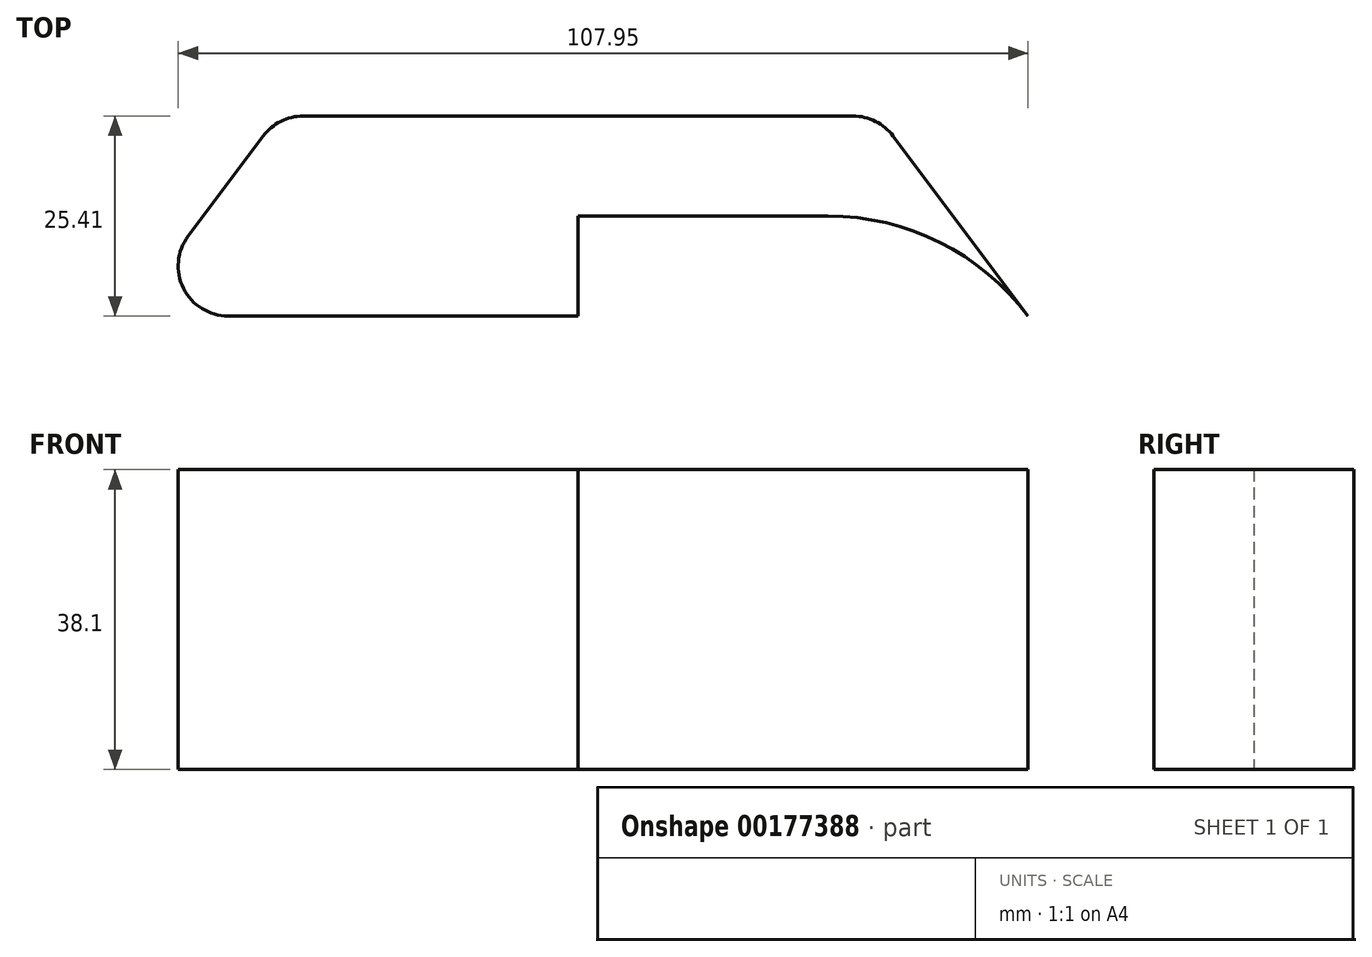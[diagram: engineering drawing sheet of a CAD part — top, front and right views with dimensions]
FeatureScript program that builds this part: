
annotation { "Feature Type Name" : "Feature", "Feature Type Description" : "" }
export const myFeature = defineFeature(function(context is Context, id is Id, definition is map)
    precondition{}
    {
        {
            var Q0;
            Q0=qCreatedBy(makeId("Top.planeOp"),FACE);
            var sketch = newSketch(context, id + "F0", { "sketchPlane" : qUnion([Q0])});
            skLineSegment(sketch, "E0.bottom", {"start": v(58.8, 47.63) * mm, "end": v(-58.8, 47.63) * mm});
            skLineSegment(sketch, "E0.top", {"start": v(58.8, -47.62) * mm, "end": v(-58.8, -47.62) * mm});
            skLineSegment(sketch, "E0.left", {"start": v(58.8, 47.63) * mm, "end": v(58.8, -47.62) * mm});
            skLineSegment(sketch, "E0.right", {"start": v(-58.8, 47.63) * mm, "end": v(-58.8, -47.62) * mm});
            skPoint(sketch, "E0.middle", {"position": v(0, 0) * mm});
            skLineSegment(sketch, "E1", {"start": v(0, 47.63) * mm, "end": v(0, 15.88) * mm});
            skPoint(sketch, "E1.endSnap0", {"position": v(0, 47.63) * mm});
            skLineSegment(sketch, "E2", {"start": v(0, 15.88) * mm, "end": v(31.75, 15.88) * mm});
            skLineSegment(sketch, "E3.MirrorCS", {"start": v(0, 15.88) * mm, "end": v(-31.75, 15.88) * mm});
            skArc(sketch, "E4", {"start": v(-31.75, 47.63) * mm, "mid": v(-63.5, 15.88) * mm, "end": v(-31.75, -15.87) * mm});
            skArc(sketch, "E5", {"start": v(31.75, 47.63) * mm, "mid": v(63.5, 15.88) * mm, "end": v(31.75, -15.87) * mm});
            skLineSegment(sketch, "E6", {"start": v(0, -47.62) * mm, "end": v(-50.8, -47.62) * mm});
            skLineSegment(sketch, "E7.MirrorCS", {"start": v(0, -47.62) * mm, "end": v(50.8, -47.62) * mm});
            skLineSegment(sketch, "E8", {"start": v(0, 47.63) * mm, "end": v(0, 60.33) * mm});
            skLineSegment(sketch, "E9", {"start": v(0, 60.33) * mm, "end": v(38.1, 60.33) * mm});
            skLineSegment(sketch, "E10.MirrorCS", {"start": v(0, 60.33) * mm, "end": v(-38.1, 60.33) * mm});
            skLineSegment(sketch, "E11", {"start": v(38.1, 60.33) * mm, "end": v(57.15, 34.93) * mm});
            skLineSegment(sketch, "E12", {"start": v(57.15, 34.93) * mm, "end": v(-57.15, 34.93) * mm});
            skLineSegment(sketch, "E13", {"start": v(-57.15, 34.93) * mm, "end": v(-38.1, 60.33) * mm});
            skLineSegment(sketch, "E14", {"start": v(-50.8, -47.62) * mm, "end": v(-50.8, -9.52) * mm});
            skLineSegment(sketch, "E15", {"start": v(50.8, -47.62) * mm, "end": v(50.8, -9.52) * mm});
            skSolve(sketch);
        }
        {
            var Q0;
            {var subQ1=sQuery(id+"F0.wireOp",EDGE,"E8");Q0=makeQuery(id+"F0.imprint","IMPRINT",FACE,{"disambiguationData":[TD([[makeQuery(id+"F0.imprint","IMPRINT",EDGE,{"derivedFrom":subQ1}),1.0]])]});}
            var Q1;
            {var subQ5=sQuery(id+"F0.wireOp",EDGE,"E8");Q1=makeQuery(id+"F0.imprint","IMPRINT",FACE,{"disambiguationData":[TD([[makeQuery(id+"F0.imprint","IMPRINT",EDGE,{"derivedFrom":subQ5}),-1.0]])]});}
            var Q2;
            {var subQ0=sQuery(id+"F0.wireOp",EDGE,"E4");var subQ1=sQuery(id+"F0.wireOp",EDGE,"E0.bottom");var subQ2=makeQuery(id+"F0.imprint","INTERSECT",VERTEX,{"derivedFrom":[subQ1,subQ0]});Q2=makeQuery(id+"F0.imprint","IMPRINT",FACE,{"disambiguationData":[TD([[makeQuery(id+"F0.imprint","IMPRINT",EDGE,{"disambiguationData":[TD([[subQ2,-1.0]])],"derivedFrom":subQ1}),1.0]])]});}
            var Q3;
            {var subQ1=sQuery(id+"F0.wireOp",EDGE,"E0.bottom");var subQ3=sQuery(id+"F0.wireOp",EDGE,"E4");var subQ4=makeQuery(id+"F0.imprint","INTERSECT",VERTEX,{"derivedFrom":[subQ1,subQ3]});Q3=makeQuery(id+"F0.imprint","IMPRINT",FACE,{"disambiguationData":[TD([[makeQuery(id+"F0.imprint","IMPRINT",EDGE,{"disambiguationData":[TD([[subQ4,1.0]])],"derivedFrom":subQ1}),1.0]])]});}
            var Q4;
            {var subQ1=sQuery(id+"F0.wireOp",EDGE,"E0.bottom");var subQ3=sQuery(id+"F0.wireOp",EDGE,"E5");var subQ4=makeQuery(id+"F0.imprint","INTERSECT",VERTEX,{"derivedFrom":[subQ1,subQ3]});Q4=makeQuery(id+"F0.imprint","IMPRINT",FACE,{"disambiguationData":[TD([[makeQuery(id+"F0.imprint","IMPRINT",EDGE,{"disambiguationData":[TD([[subQ4,-1.0]])],"derivedFrom":subQ3}),-1.0]])]});}
            var Q5;
            {var subQ0=sQuery(id+"F0.wireOp",EDGE,"E5");var subQ1=sQuery(id+"F0.wireOp",EDGE,"E0.bottom");var subQ2=makeQuery(id+"F0.imprint","INTERSECT",VERTEX,{"derivedFrom":[subQ1,subQ0]});Q5=makeQuery(id+"F0.imprint","IMPRINT",FACE,{"disambiguationData":[TD([[makeQuery(id+"F0.imprint","IMPRINT",EDGE,{"disambiguationData":[TD([[subQ2,1.0]])],"derivedFrom":subQ1}),1.0]])]});}
            var Q6;
            {var subQ9=sQuery(id+"F0.wireOp",EDGE,"E6");Q6=makeQuery(id+"F0.imprint","IMPRINT",FACE,{"disambiguationData":[TD([[makeQuery(id+"F0.imprint","IMPRINT",EDGE,{"derivedFrom":subQ9}),-1.0]])]});}
            var Q7;
            {var subQ0=sQuery(id+"F0.wireOp",EDGE,"E5");var subQ1=sQuery(id+"F0.wireOp",EDGE,"E0.left");var subQ2=makeQuery(id+"F0.imprint","INTERSECT",VERTEX,{"disambiguationData":[OD(0.0)],"derivedFrom":[subQ1,subQ0]});Q7=makeQuery(id+"F0.imprint","IMPRINT",FACE,{"disambiguationData":[TD([[makeQuery(id+"F0.imprint","IMPRINT",EDGE,{"disambiguationData":[TD([[subQ2,-1.0]])],"derivedFrom":subQ1}),1.0]])]});}
            var Q8;
            {var subQ0=sQuery(id+"F0.wireOp",EDGE,"E4");var subQ1=sQuery(id+"F0.wireOp",EDGE,"E0.right");var subQ2=makeQuery(id+"F0.imprint","INTERSECT",VERTEX,{"disambiguationData":[OD(0.0)],"derivedFrom":[subQ1,subQ0]});Q8=makeQuery(id+"F0.imprint","IMPRINT",FACE,{"disambiguationData":[TD([[makeQuery(id+"F0.imprint","IMPRINT",EDGE,{"disambiguationData":[TD([[subQ2,-1.0]])],"derivedFrom":subQ1}),-1.0]])]});}
            extrude(context, id + "F1", {"entities" : qUnion([Q0, Q1, Q2, Q3, Q4, Q5, Q6, Q7, Q8]), "depth" : 38.1 * mm});
        }
        {
            var Q0;
            Q0=makeQuery(id+"F1.opExtrude","SWEPT_EDGE",EDGE,{"disambiguationData":[OSD([sQuery(id+"F0.wireOp",EDGE,"E0.top"),sQuery(id+"F0.wireOp",EDGE,"E6"),sQuery(id+"F0.wireOp",EDGE,"E14")])]});
            var Q1;
            Q1=makeQuery(id+"F1.opExtrude","SWEPT_EDGE",EDGE,{"disambiguationData":[OSD([sQuery(id+"F0.wireOp",EDGE,"E0.top"),sQuery(id+"F0.wireOp",EDGE,"E7.MirrorCS"),sQuery(id+"F0.wireOp",EDGE,"E15")])]});
            var Q2;
            Q2=makeQuery(id+"F1.opExtrude","SWEPT_EDGE",EDGE,{"disambiguationData":[OSD([sQuery(id+"F0.wireOp",EDGE,"E5"),sQuery(id+"F0.wireOp",EDGE,"E15")])]});
            var Q3;
            Q3=makeQuery(id+"F1.opExtrude","SWEPT_EDGE",EDGE,{"disambiguationData":[OSD([sQuery(id+"F0.wireOp",EDGE,"E4"),sQuery(id+"F0.wireOp",EDGE,"E14")])]});
            var Q4;
            Q4=makeQuery(id+"F1.opExtrude","SWEPT_EDGE",EDGE,{"disambiguationData":[OSD([sQuery(id+"F0.wireOp",EDGE,"E10.MirrorCS"),sQuery(id+"F0.wireOp",EDGE,"E13")])]});
            var Q5;
            Q5=makeQuery(id+"F1.opExtrude","SWEPT_EDGE",EDGE,{"disambiguationData":[OSD([sQuery(id+"F0.wireOp",EDGE,"E9"),sQuery(id+"F0.wireOp",EDGE,"E11")])]});
            fillet(context, id + "F2", {"entities" : qUnion([Q0, Q1, Q2, Q3, Q4, Q5]), "radius" : 6.35 * mm, "tangentPropagation" : true, "allowEdgeOverflow" : false});
        }
    });
